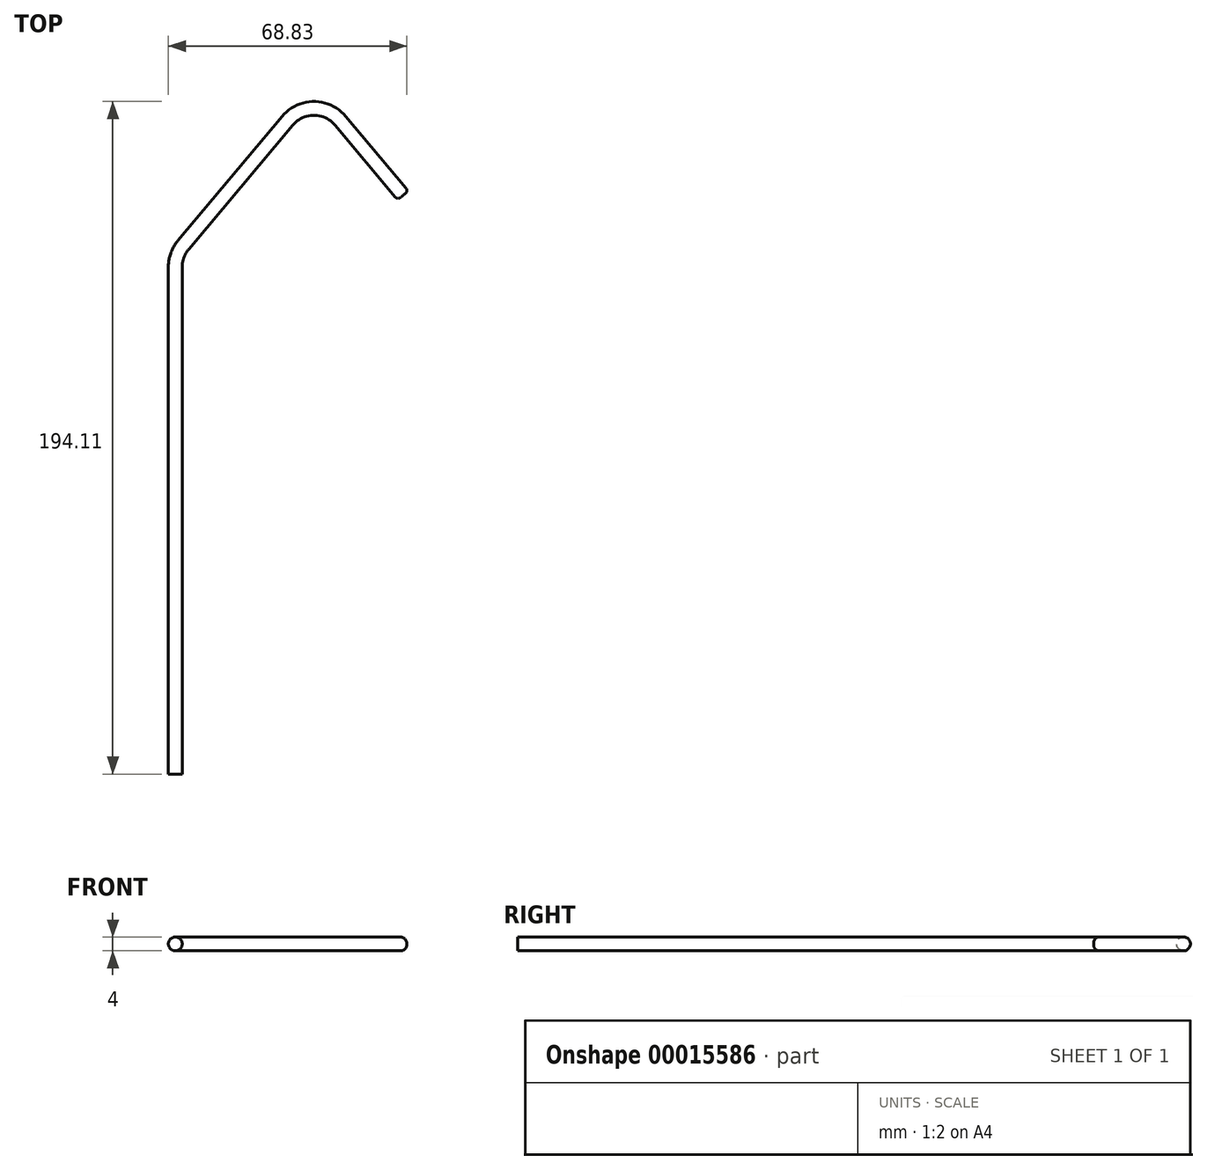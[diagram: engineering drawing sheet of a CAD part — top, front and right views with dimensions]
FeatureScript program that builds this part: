
annotation { "Feature Type Name" : "Feature", "Feature Type Description" : "" }
export const myFeature = defineFeature(function(context is Context, id is Id, definition is map)
    precondition{}
    {
        {
            var Q0;
            Q0=qCreatedBy(makeId("Top.planeOp"),FACE);
            var sketch = newSketch(context, id + "F0", { "sketchPlane" : qUnion([Q0])});
            skLineSegment(sketch, "E0", {"start": v(0, 0) * mm, "end": v(0, 146.36) * mm});
            skLineSegment(sketch, "E1", {"start": v(2.34, 152.79) * mm, "end": v(32.34, 188.54) * mm});
            skLineSegment(sketch, "E2", {"start": v(47.66, 188.54) * mm, "end": v(65.71, 167.03) * mm});
            skLineSegment(sketch, "E3", {"start": v(40, 213.26) * mm, "end": v(40, 172.58) * mm, "construction": true});
            skPoint(sketch, "E4.visualSharp", {"position": v(0, 150) * mm});
            skArc(sketch, "E4.filletArc", {"start": v(2.34, 152.79) * mm, "mid": v(0.6, 149.78) * mm, "end": v(0, 146.36) * mm});
            skPoint(sketch, "E5.visualSharp", {"position": v(40, 197.67) * mm});
            skArc(sketch, "E5.filletArc", {"start": v(47.66, 188.54) * mm, "mid": v(40, 192.11) * mm, "end": v(32.34, 188.54) * mm});
            skSolve(sketch);
        }
        {
            var Q0;
            Q0=qCreatedBy(makeId("Front.planeOp"),FACE);
            var sketch = newSketch(context, id + "F1", { "sketchPlane" : qUnion([Q0])});
            skCircle(sketch, "E6", {"center": v(0, 0) * mm, "radius": 2 * mm});
            skSolve(sketch);
        }
        {
            var Q0;
            Q0=makeQuery(id+"F1.imprint","IMPRINT",FACE,{"disambiguationData":[TD([[makeQuery(id+"F1.imprint","IMPRINT",EDGE,{"derivedFrom":sQuery(id+"F1.wireOp",EDGE,"E6")}),1.0]])]});
            var Q1;
            Q1=sQuery(id+"F0.wireOp",EDGE,"E0");
            var Q2;
            Q2=sQuery(id+"F0.wireOp",EDGE,"E4.filletArc");
            var Q3;
            Q3=sQuery(id+"F0.wireOp",EDGE,"E1");
            var Q4;
            Q4=sQuery(id+"F0.wireOp",EDGE,"E5.filletArc");
            var Q5;
            Q5=sQuery(id+"F0.wireOp",EDGE,"E2");
            sweep(context, id + "F2", {"profiles" : qUnion([Q0]), "path" : qUnion([Q1, Q2, Q3, Q4, Q5])});
        }
        {
            var Q0;
            Q0=makeQuery(id+"F2.opSweep","CAP_EDGE",EDGE,{"disambiguationData":[OSD([sQuery(id+"F0.wireOp",VERTEX,"E2.end"),sQuery(id+"F1.wireOp",EDGE,"E6")])],"isStart":false});
            fillet(context, id + "F3", {"entities" : qUnion([Q0]), "radius" : 1 * mm, "tangentPropagation" : true, "allowEdgeOverflow" : false});
        }
    });
